# Revit family: LAMP_KOMBIC SURFACE
name_source: partatom
category: Luminarias
revit_build: Autodesk Revit 2018 (Build: 20190510_1515(x64)
units: mm (PartAtom-declared; Revit-internal decimal feet)

## family parameters
Anfitrión = Techo
Compartido = No
Corte con vacíos al cargar = No
Cota de conector redondo = Diámetro de uso
Número OmniClass = 23.80.70.11
Origen de luz = Sí
Punto de cálculo de habitación = No
Siempre vertical = Sí
Tipo de pieza = Normal
Título OmniClass = Luminaries for Internal Lighting

## types (8) — shared parameters
Altura Kombic sur. = 230 mm  [stored 0.754593 ft]
CRI = 80
Cambio de temperatura de color de luz atenuada = <Ninguno>
Diam. Kombic sur. = 197 mm
Dimensions = Ø197mm x 230mm
Fabricante = LAMP
Filtro de color = 16777215
Finish = RAL9010
Gear = Electronic
IEE = A+
Installation instructions = https://www.lamp.es
Insulation class = II
LED Lifetime = 50.000 L80 B10
Last update = 24/02/2022
Lámpara = MID-POWER LED
MacAdam = 3
Manufacturer URL = http://www.lamp.es
Manufacturer country = Spain
Manufacturer name = LAMP
Material Cables = LAMP_Acero genérico
Material Difusor = LAMP_PMMA Difusor Kombic
Material Reflector = LAMP_PC Reflector Kombic Metalizado Brillante
Material Tija = LAMP_Plástico genérico
Photobiological risk = Group 0
Power Supply = 220-240V 50/60Hz
Product URL = https://www.lamp.es
Product datasheet = http://www.lamp.es
Protection rating = IP20
Type = MID POWER TRIDONIC
Ángulo de inclinación = 90.00°

## per-type parameters (varying)
| type | Archivo de red fotométrica | Descripción | Efficacy | Material Armazón | Modelo | Plum | Power | Product code | Weight |
| 2065LM 3000 BRIGHT NEGRO | K31SF3020OP830NRW.IES | KOMBIC 200 SF 3000 IP20 WW OPAL BR/BK | 115 lm/W | LAMP_PC Armazón Kombic NG | K31SF3020OP830NRB | 18 W | 17 W | K31SF3020OP830NRB | 1.62 kg |
| 2065LM 3000 BRIGHT BLANCO | K31SF3020OP830NRB.IES | KOMBIC 200 SF 3000 IP20 WW OPAL BR/WH | 115 lm/W | LAMP_PC Armazón Kombic BL | K31SF3020OP830NRW | 18 W | 17 W | K31SF3020OP830NRW | 1.62 kg |
| 2171LM 4000 BRIGHT NEGRO | K31SF3020OP840NRW.IES | KOMBIC 200 SF 3000 IP20 NW OPAL BR/BK | 121 lm/W | LAMP_PC Armazón Kombic NG | K31SF3020OP840NRB | 18 W | 17 W | K31SF3020OP840NRB | 1.62 kg |
| 2171LM 4000 BRIGHT BLANCO | K31SF3020OP840NRB.IES | KOMBIC 200 SF 3000 IP20 NW OPAL BR/WH | 121 lm/W | LAMP_PC Armazón Kombic BL | K31SF3020OP840NRW | 18 W | 17 W | K31SF3020OP840NRW | 1.62 kg |
| 2800LM 3000 BRIGHT NEGRO | K31SF4020OP830NRW.IES | KOMBIC 200 SF 4000 IP20 WW OPAL BR/BK | 109 lm/W | LAMP_PC Armazón Kombic NG | K31SF4020OP830NRB | 26 W | 24 W | K31SF4020OP830NRB | 2.26 kg |
| 2800LM 3000 BRIGHT BLANCO | K31SF4020OP830NRB.IES | KOMBIC 200 SF 4000 IP20 WW OPAL BR/WH | 109 lm/W | LAMP_PC Armazón Kombic BL | K31SF4020OP830NRW | 26 W | 24 W | K31SF4020OP830NRW | 2.26 kg |
| 2944LM 4000 BRIGHT NEGRO | K31SF4020OP840NRW.IES | KOMBIC 200 SF 4000 IP20 NW OPAL BR/BK | 114 lm/W | LAMP_PC Armazón Kombic NG | K31SF4020OP840NRB | 26 W | 24 W | K31SF4020OP840NRB | 2.26 kg |
| 2944LM 4000 BRIGHT BLANCO | K31SF4020OP840NRB.IES | KOMBIC 200 SF 4000 IP20 NW OPAL BR/WH | 114 lm/W | LAMP_PC Armazón Kombic BL | K31SF4020OP840NRW | 26 W | 24 W | K31SF4020OP840NRW | 2.26 kg |

note: [stored X ft] marks values corroborated as IEEE doubles in the binary element streams (Revit-internal decimal feet)

## geometry (parser evidence)
native form markers: Blend x2
no freeform markers — native parametric forms only
